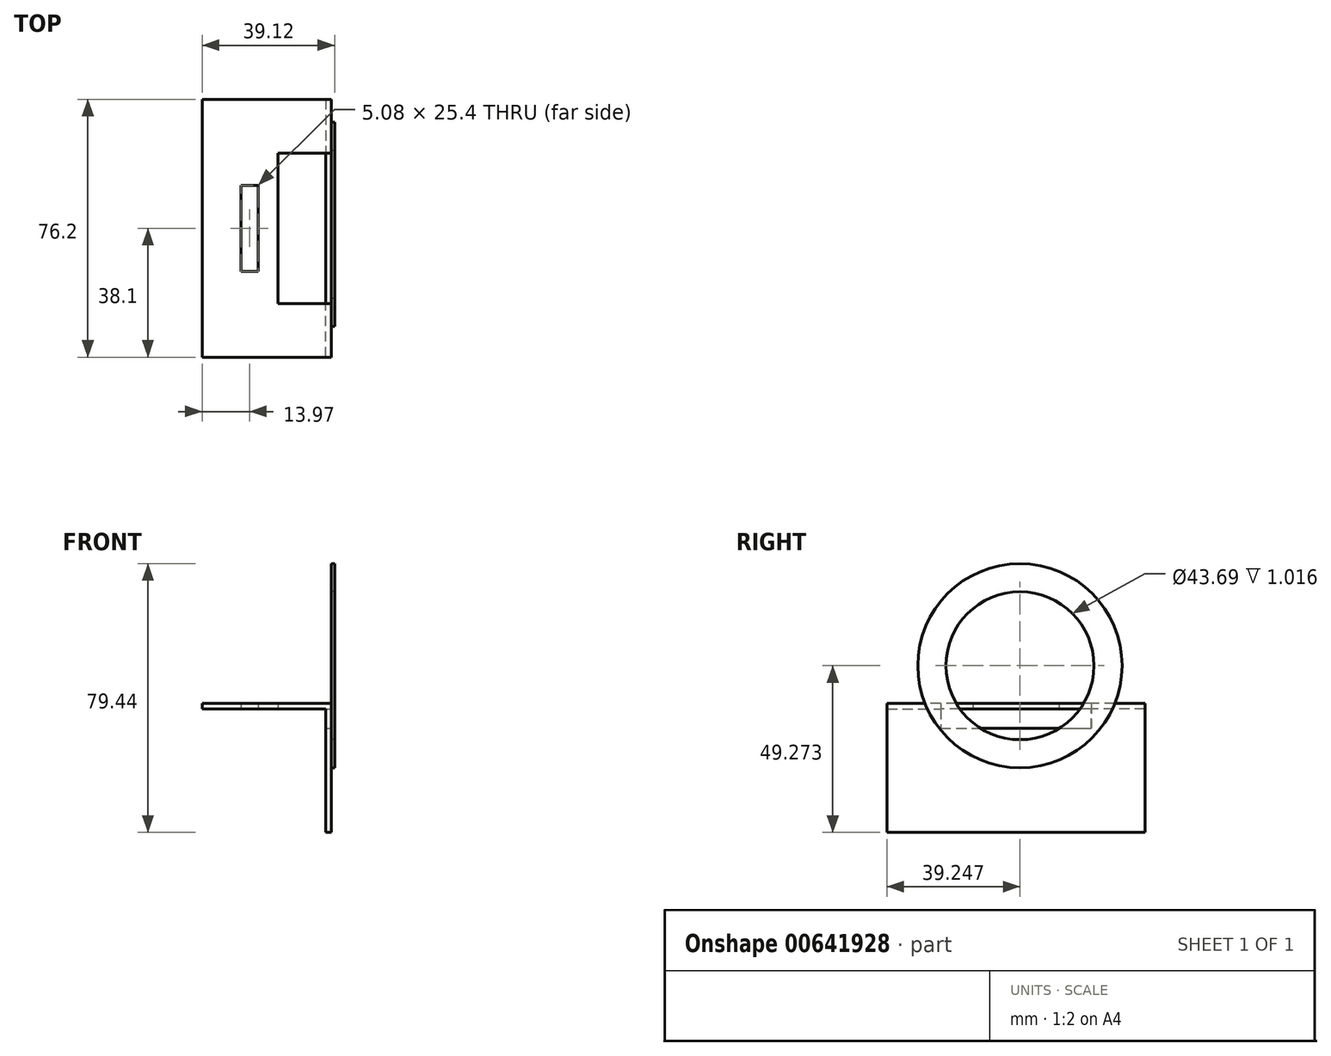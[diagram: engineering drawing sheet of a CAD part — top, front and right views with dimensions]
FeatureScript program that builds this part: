
annotation { "Feature Type Name" : "Feature", "Feature Type Description" : "" }
export const myFeature = defineFeature(function(context is Context, id is Id, definition is map)
    precondition{}
    {
        {
            var Q0;
            Q0=qCreatedBy(makeId("Top.planeOp"),FACE);
            var sketch = newSketch(context, id + "F0", { "sketchPlane" : qUnion([Q0])});
            skLineSegment(sketch, "E0.bottom", {"start": v(0, 0) * mm, "end": v(38.1, 0) * mm});
            skLineSegment(sketch, "E0.top", {"start": v(0, -76.2) * mm, "end": v(38.1, -76.2) * mm});
            skLineSegment(sketch, "E0.left", {"start": v(0, 0) * mm, "end": v(0, -76.2) * mm});
            skLineSegment(sketch, "E0.right", {"start": v(38.1, 0) * mm, "end": v(38.1, -15.88) * mm});
            skLineSegment(sketch, "E1.bottom", {"start": v(11.43, -25.4) * mm, "end": v(16.51, -25.4) * mm});
            skLineSegment(sketch, "E1.top", {"start": v(11.43, -50.8) * mm, "end": v(16.51, -50.8) * mm});
            skLineSegment(sketch, "E1.left", {"start": v(11.43, -25.4) * mm, "end": v(11.43, -50.8) * mm});
            skLineSegment(sketch, "E1.right", {"start": v(16.51, -25.4) * mm, "end": v(16.51, -50.8) * mm});
            skPoint(sketch, "E2", {"position": v(11.43, -38.1) * mm});
            skPoint(sketch, "E3", {"position": v(0, -38.1) * mm});
            skLineSegment(sketch, "E4", {"start": v(38.1, -15.88) * mm, "end": v(22.35, -15.88) * mm});
            skLineSegment(sketch, "E5", {"start": v(22.35, -15.88) * mm, "end": v(22.35, -60.33) * mm});
            skLineSegment(sketch, "E6", {"start": v(22.35, -60.33) * mm, "end": v(38.1, -60.33) * mm});
            skPoint(sketch, "E7", {"position": v(22.35, -38.1) * mm});
            skLineSegment(sketch, "E8.trimOffspring", {"start": v(38.1, -60.33) * mm, "end": v(38.1, -76.2) * mm});
            skSolve(sketch);
        }
        {
            var Q0;
            Q0 = qSketchRegion(id + "F0", true);
            extrude(context, id + "F1", {"entities" : qUnion([Q0]), "depth" : 1.59 * mm, "offsetDistance" : 25.4 * mm});
        }
        {
            var Q0;
            Q0=makeQuery(id+"F1.opExtrude","SWEPT_FACE",FACE,{"disambiguationData":[OSD([sQuery(id+"F0.wireOp",EDGE,"E0.right")])]});
            var sketch = newSketch(context, id + "F2", { "sketchPlane" : qUnion([Q0])});
            skLineSegment(sketch, "E9.bottom", {"start": v(0, 1.59) * mm, "end": v(-15.88, 1.59) * mm});
            skLineSegment(sketch, "E9.top", {"start": v(0, -36.51) * mm, "end": v(-76.2, -36.51) * mm});
            skLineSegment(sketch, "E9.left", {"start": v(0, 1.59) * mm, "end": v(0, -36.51) * mm});
            skLineSegment(sketch, "E9.right", {"start": v(-76.2, 1.59) * mm, "end": v(-76.2, -36.51) * mm});
            skLineSegment(sketch, "E10", {"start": v(-60.36, 1.59) * mm, "end": v(-60.36, -5.78) * mm});
            skLineSegment(sketch, "E11", {"start": v(-60.36, -5.78) * mm, "end": v(-15.88, -5.78) * mm});
            skLineSegment(sketch, "E12", {"start": v(-15.88, -5.78) * mm, "end": v(-15.88, 1.59) * mm});
            skLineSegment(sketch, "E13.trimOffspring", {"start": v(-60.36, 1.59) * mm, "end": v(-76.2, 1.59) * mm});
            skSolve(sketch);
        }
        {
            var Q0;
            {var subQ13=sQuery(id+"F2.wireOp",EDGE,"E9.top");Q0=makeQuery(id+"F2.imprint","IMPRINT",FACE,{"disambiguationData":[TD([[makeQuery(id+"F2.imprint","IMPRINT",EDGE,{"derivedFrom":subQ13}),-1.0]])]});}
            var Q1;
            {var subQ0=sQuery(id+"F2.wireOp",EDGE,"E13.trimOffspring");var subQ1=sQuery(id+"F2.wireOp",EDGE,"E10");var subQ2=makeQuery(id+"F2.imprint","INTERSECT",VERTEX,{"derivedFrom":[subQ1,subQ0]});Q1=makeQuery(id+"F2.imprint","IMPRINT",FACE,{"disambiguationData":[TD([[makeQuery(id+"F2.imprint","IMPRINT",EDGE,{"disambiguationData":[TD([[subQ2,-1.0]])],"derivedFrom":subQ1}),-1.0]])]});}
            var Q2;
            {var subQ0=sQuery(id+"F2.wireOp",EDGE,"E12");var subQ3=sQuery(id+"F2.wireOp",EDGE,"5YyeplCm-LCnA-jkbf-Zlpj-ZgRNDM1lt9KY");var subQ4=makeQuery(id+"F2.imprint","INTERSECT",VERTEX,{"derivedFrom":[subQ0,subQ3]});Q2=makeQuery(id+"F2.imprint","IMPRINT",FACE,{"disambiguationData":[TD([[makeQuery(id+"F2.imprint","IMPRINT",EDGE,{"disambiguationData":[TD([[subQ4,-1.0]])],"derivedFrom":subQ0}),-1.0]])]});}
            var Q3;
            {var subQ0=sQuery(id+"F2.wireOp",EDGE,"5YyeplCm-LCnA-jkbf-Zlpj-ZgRNDM1lt9KY");var subQ1=sQuery(id+"F2.wireOp",EDGE,"E11");var subQ2=makeQuery(id+"F2.imprint","INTERSECT",VERTEX,{"disambiguationData":[OD(0.0)],"derivedFrom":[subQ1,subQ0]});Q3=makeQuery(id+"F2.imprint","IMPRINT",FACE,{"disambiguationData":[TD([[makeQuery(id+"F2.imprint","IMPRINT",EDGE,{"disambiguationData":[TD([[subQ2,-1.0]])],"derivedFrom":subQ1}),-1.0]])]});}
            extrude(context, id + "F3", {"entities" : qUnion([Q0, Q1, Q2, Q3]), "operationType" : NewBodyOperationType.ADD, "oppositeDirection" : true, "depth" : 1.59 * mm, "offsetDistance" : 25.4 * mm});
        }
        {
            var Q0;
            {var subQ0=sQuery(id+"F0.wireOp",EDGE,"E0.right");Q0=makeQuery(id+"F3.boolean.opBoolean","MERGE",FACE,{"derivedFrom":[makeQuery(id+"F1.opExtrude","SWEPT_FACE",FACE,{"disambiguationData":[OSD([subQ0])]}),makeQuery(id+"F1.opExtrude","SWEPT_FACE",FACE,{"disambiguationData":[OSD([sQuery(id+"F0.wireOp",EDGE,"E8.trimOffspring")])]}),makeQuery(id+"F3.opExtrude","CAP_FACE",FACE,{"disambiguationData":[OSD([subQ0,sQuery(id+"F2.wireOp",EDGE,"E9.top"),sQuery(id+"F2.wireOp",EDGE,"E9.left"),sQuery(id+"F2.wireOp",EDGE,"E9.right"),sQuery(id+"F2.wireOp",EDGE,"E10"),sQuery(id+"F2.wireOp",EDGE,"E11"),sQuery(id+"F2.wireOp",EDGE,"E12"),sQuery(id+"F2.wireOp",EDGE,"E13.trimOffspring")])],"isStart":true})]});}
            var sketch = newSketch(context, id + "F4", { "sketchPlane" : qUnion([Q0])});
            skCircle(sketch, "E14", {"center": v(-36.95, 12.76) * mm, "radius": 30.16 * mm});
            skCircle(sketch, "E15", {"center": v(-36.95, 12.76) * mm, "radius": 21.84 * mm});
            skSolve(sketch);
        }
        {
            var Q0;
            Q0 = qSketchRegion(id + "F4", true);
            extrude(context, id + "F5", {"entities" : qUnion([Q0]), "depth" : 1.02 * mm, "offsetDistance" : 25.4 * mm});
        }
    });
